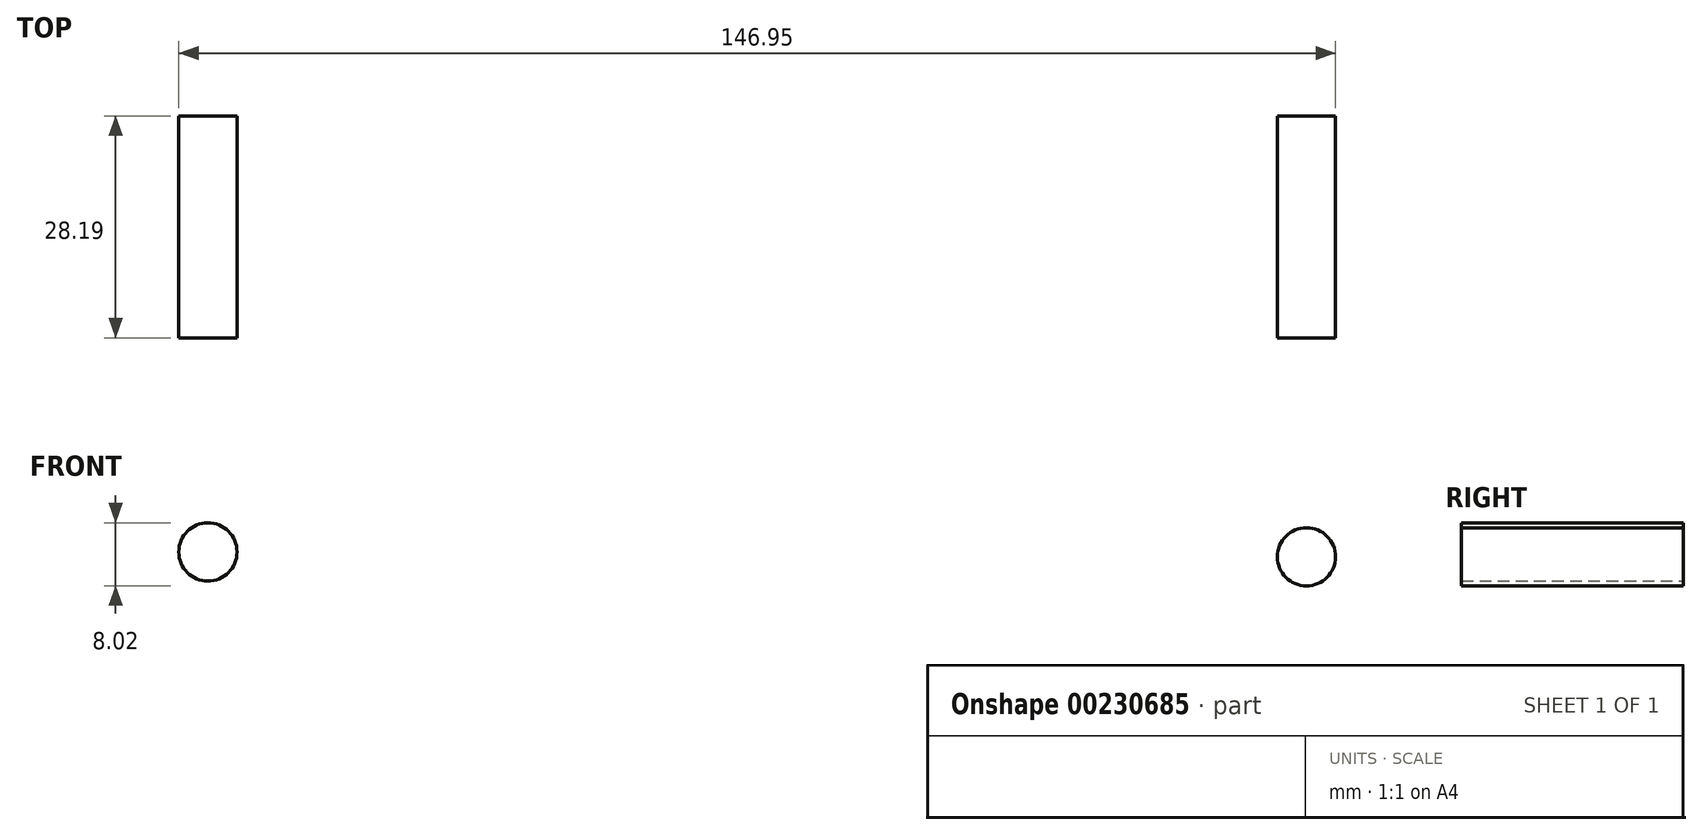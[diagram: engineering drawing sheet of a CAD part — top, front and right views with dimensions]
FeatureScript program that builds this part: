
annotation { "Feature Type Name" : "Feature", "Feature Type Description" : "" }
export const myFeature = defineFeature(function(context is Context, id is Id, definition is map)
    precondition{}
    {
        {
            var Q0;
            Q0=qCreatedBy(makeId("Front.planeOp"),FACE);
            var sketch = newSketch(context, id + "F0", { "sketchPlane" : qUnion([Q0])});
            skCircle(sketch, "E0", {"center": v(-69.88, 0) * mm, "radius": 3.7 * mm});
            skCircle(sketch, "E1", {"center": v(69.67, -0.62) * mm, "radius": 3.7 * mm});
            skSolve(sketch);
        }
        {
            var Q0;
            Q0=makeQuery(id+"F0.imprint","IMPRINT",FACE,{"disambiguationData":[TD([[makeQuery(id+"F0.imprint","IMPRINT",EDGE,{"derivedFrom":sQuery(id+"F0.wireOp",EDGE,"E0")}),1.0]])]});
            var Q1;
            Q1=makeQuery(id+"F0.imprint","IMPRINT",FACE,{"disambiguationData":[TD([[makeQuery(id+"F0.imprint","IMPRINT",EDGE,{"derivedFrom":sQuery(id+"F0.wireOp",EDGE,"E1")}),1.0]])]});
            extrude(context, id + "F1", {"entities" : qUnion([Q0, Q1]), "depth" : 28.2 * mm});
        }
    });
